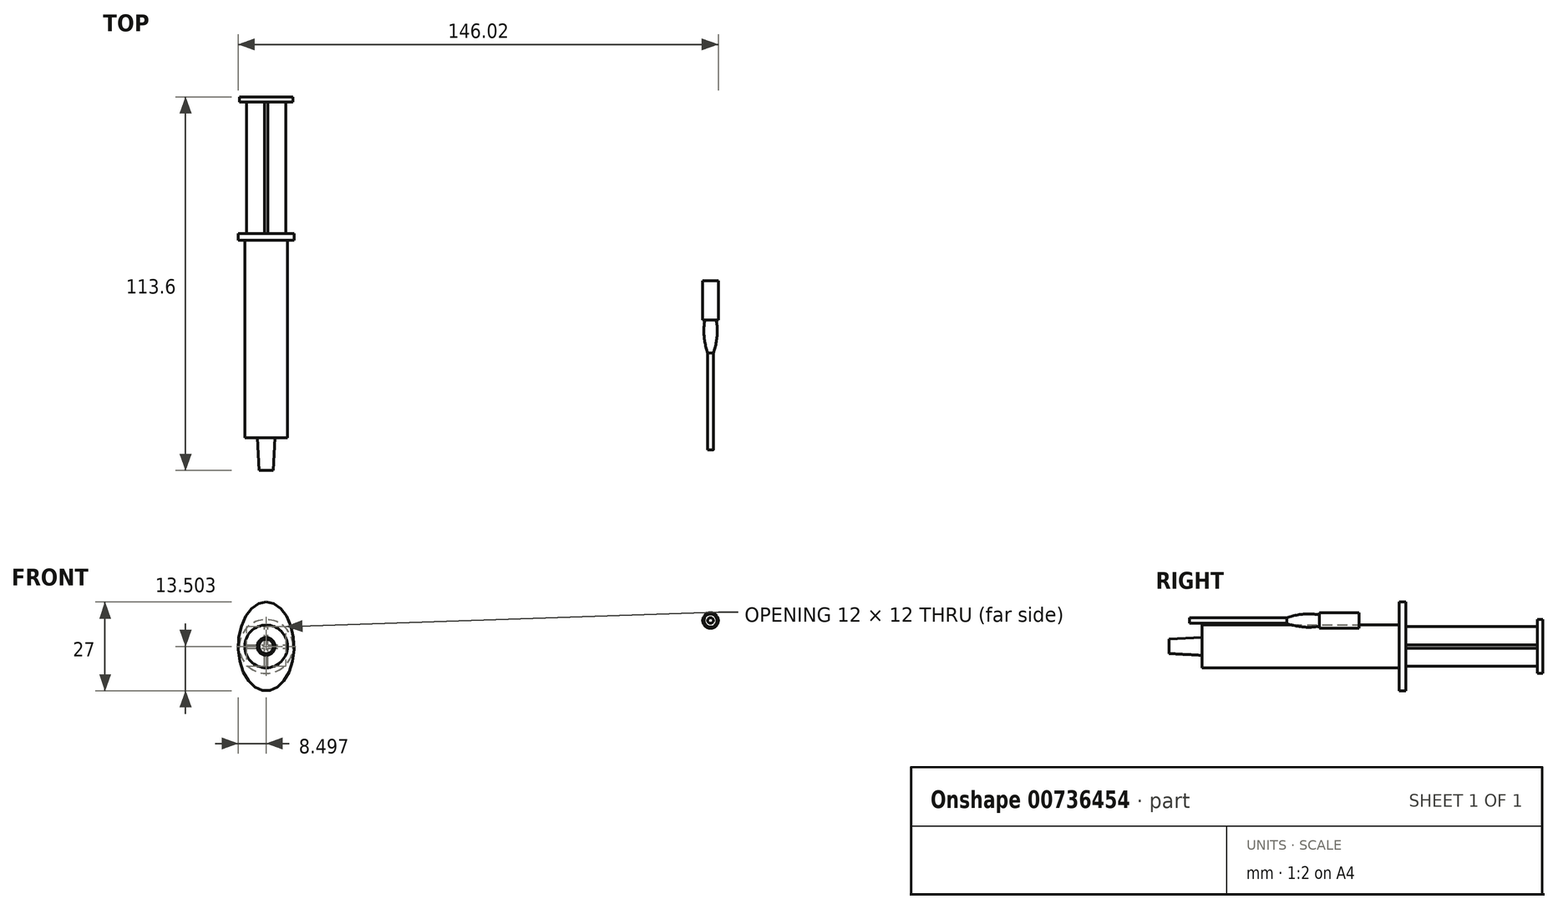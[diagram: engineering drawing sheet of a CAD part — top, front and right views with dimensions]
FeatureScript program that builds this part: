
annotation { "Feature Type Name" : "Feature", "Feature Type Description" : "" }
export const myFeature = defineFeature(function(context is Context, id is Id, definition is map)
    precondition{}
    {
        {
            var Q0;
            Q0=qCreatedBy(makeId("Front.planeOp"),FACE);
            var sketch = newSketch(context, id + "F0", { "sketchPlane" : qUnion([Q0])});
            skEllipse(sketch, "E0", {"center": v(-135.14, -7.87) * mm, "majorRadius": 13.5 * mm, "minorRadius": 8.5 * mm, "majorAxis": v(0, 1)});
            skCircle(sketch, "E1", {"center": v(-135.14, -7.87) * mm, "radius": 6.5 * mm});
            skLineSegment(sketch, "E2", {"start": v(-143.64, -7.87) * mm, "end": v(-126.64, -7.87) * mm, "construction": true});
            skLineSegment(sketch, "E3", {"start": v(-135.14, 5.63) * mm, "end": v(-135.14, -21.37) * mm, "construction": true});
            skSolve(sketch);
        }
        {
            var Q0;
            Q0=makeQuery(id+"F0.imprint","IMPRINT",FACE,{"disambiguationData":[TD([[makeQuery(id+"F0.imprint","IMPRINT",EDGE,{"derivedFrom":sQuery(id+"F0.wireOp",EDGE,"E0")}),1.0]])]});
            var Q1;
            Q1=makeQuery(id+"F0.imprint","IMPRINT",FACE,{"disambiguationData":[TD([[makeQuery(id+"F0.imprint","IMPRINT",EDGE,{"derivedFrom":sQuery(id+"F0.wireOp",EDGE,"E1")}),1.0]])]});
            extrude(context, id + "F1", {"entities" : qUnion([Q0, Q1]), "oppositeDirection" : true, "depth" : 2 * mm, "offsetDistance" : 25 * mm});
        }
        {
            var Q0;
            Q0=makeQuery(id+"F0.imprint","IMPRINT",FACE,{"disambiguationData":[TD([[makeQuery(id+"F0.imprint","IMPRINT",EDGE,{"derivedFrom":sQuery(id+"F0.wireOp",EDGE,"E1")}),1.0]])]});
            extrude(context, id + "F2", {"entities" : qUnion([Q0]), "operationType" : NewBodyOperationType.ADD, "depth" : 60 * mm, "offsetDistance" : 25 * mm});
        }
        {
            var Q0;
            Q0=makeQuery(id+"F1.opExtrude","CAP_FACE",FACE,{"disambiguationData":[OSD([sQuery(id+"F0.wireOp",EDGE,"E0")])],"isStart":false});
            var sketch = newSketch(context, id + "F3", { "sketchPlane" : qUnion([Q0])});
            skLineSegment(sketch, "E4.bottom", {"start": v(141.14, -7.37) * mm, "end": v(129.14, -7.37) * mm});
            skLineSegment(sketch, "E4.top", {"start": v(141.14, -8.37) * mm, "end": v(129.14, -8.37) * mm});
            skLineSegment(sketch, "E4.left", {"start": v(141.14, -7.37) * mm, "end": v(141.14, -8.37) * mm});
            skLineSegment(sketch, "E4.right", {"start": v(129.14, -7.37) * mm, "end": v(129.14, -8.37) * mm});
            skPoint(sketch, "E4.middle", {"position": v(135.14, -7.87) * mm});
            skLineSegment(sketch, "E5.bottom", {"start": v(135.64, -13.87) * mm, "end": v(134.64, -13.87) * mm});
            skLineSegment(sketch, "E5.top", {"start": v(135.64, -1.87) * mm, "end": v(134.64, -1.87) * mm});
            skLineSegment(sketch, "E5.left", {"start": v(135.64, -13.87) * mm, "end": v(135.64, -1.87) * mm});
            skLineSegment(sketch, "E5.right", {"start": v(134.64, -13.87) * mm, "end": v(134.64, -1.87) * mm});
            skSolve(sketch);
        }
        {
            var Q0;
            {var subQ0=sQuery(id+"F3.wireOp",EDGE,"E5.left");var subQ1=sQuery(id+"F3.wireOp",EDGE,"E4.bottom");var subQ2=makeQuery(id+"F3.imprint","INTERSECT",VERTEX,{"derivedFrom":[subQ1,subQ0]});Q0=makeQuery(id+"F3.imprint","IMPRINT",FACE,{"disambiguationData":[TD([[makeQuery(id+"F3.imprint","IMPRINT",EDGE,{"disambiguationData":[TD([[subQ2,-1.0]])],"derivedFrom":subQ1}),1.0]])]});}
            var Q1;
            {var subQ5=sQuery(id+"F3.wireOp",EDGE,"E5.top");Q1=makeQuery(id+"F3.imprint","IMPRINT",FACE,{"disambiguationData":[TD([[makeQuery(id+"F3.imprint","IMPRINT",EDGE,{"derivedFrom":subQ5}),1.0]])]});}
            var Q2;
            {var subQ0=sQuery(id+"F3.wireOp",EDGE,"E4.left");Q2=makeQuery(id+"F3.imprint","IMPRINT",FACE,{"disambiguationData":[TD([[makeQuery(id+"F3.imprint","IMPRINT",EDGE,{"derivedFrom":subQ0}),-1.0]])]});}
            var Q3;
            {var subQ5=sQuery(id+"F3.wireOp",EDGE,"E5.bottom");Q3=makeQuery(id+"F3.imprint","IMPRINT",FACE,{"disambiguationData":[TD([[makeQuery(id+"F3.imprint","IMPRINT",EDGE,{"derivedFrom":subQ5}),-1.0]])]});}
            var Q4;
            {var subQ0=sQuery(id+"F3.wireOp",EDGE,"E4.right");Q4=makeQuery(id+"F3.imprint","IMPRINT",FACE,{"disambiguationData":[TD([[makeQuery(id+"F3.imprint","IMPRINT",EDGE,{"derivedFrom":subQ0}),1.0]])]});}
            extrude(context, id + "F4", {"entities" : qUnion([Q0, Q1, Q2, Q3, Q4]), "operationType" : NewBodyOperationType.ADD, "depth" : 40 * mm, "offsetDistance" : 25 * mm});
        }
        {
            var Q0;
            Q0=makeQuery(id+"F4.opExtrude","CAP_FACE",FACE,{"disambiguationData":[OSD([sQuery(id+"F3.wireOp",EDGE,"E4.bottom"),sQuery(id+"F3.wireOp",EDGE,"E4.top"),sQuery(id+"F3.wireOp",EDGE,"E4.left"),sQuery(id+"F3.wireOp",EDGE,"E4.right"),sQuery(id+"F3.wireOp",EDGE,"E5.bottom"),sQuery(id+"F3.wireOp",EDGE,"E5.top"),sQuery(id+"F3.wireOp",EDGE,"E5.left"),sQuery(id+"F3.wireOp",EDGE,"E5.right")])],"isStart":false});
            var sketch = newSketch(context, id + "F5", { "sketchPlane" : qUnion([Q0])});
            skCircle(sketch, "E6", {"center": v(135.14, -7.87) * mm, "radius": 8.17 * mm});
            skSolve(sketch);
        }
        {
            var Q0;
            Q0=makeQuery(id+"F5.imprint","IMPRINT",FACE,{"disambiguationData":[TD([[makeQuery(id+"F5.imprint","IMPRINT",EDGE,{"derivedFrom":sQuery(id+"F5.wireOp",EDGE,"E6")}),1.0]])]});
            var Q1;
            {var subQ8=sQuery(id+"F3.wireOp",EDGE,"E4.left");Q1=makeQuery(id+"F5.imprint","IMPRINT",FACE,{"disambiguationData":[TD([[makeQuery(id+"F5.imprint","IMPRINT",EDGE,{"derivedFrom":makeQuery(id+"F4.opExtrude","CAP_EDGE",EDGE,{"disambiguationData":[OSD([subQ8])],"isStart":false})}),-1.0]])]});}
            extrude(context, id + "F6", {"entities" : qUnion([Q0, Q1]), "operationType" : NewBodyOperationType.ADD, "depth" : 1.6 * mm, "offsetDistance" : 25 * mm});
        }
        {
            var Q0;
            Q0=makeQuery(id+"F2.opExtrude","CAP_FACE",FACE,{"disambiguationData":[OSD([sQuery(id+"F0.wireOp",EDGE,"E1")])],"isStart":false});
            var sketch = newSketch(context, id + "F7", { "sketchPlane" : qUnion([Q0])});
            skCircle(sketch, "E7", {"center": v(-135.14, -7.87) * mm, "radius": 2.7 * mm});
            skSolve(sketch);
        }
        {
            var Q0;
            Q0=makeQuery(id+"F7.imprint","IMPRINT",FACE,{"disambiguationData":[TD([[makeQuery(id+"F7.imprint","IMPRINT",EDGE,{"derivedFrom":sQuery(id+"F7.wireOp",EDGE,"E7")}),1.0]])]});
            extrude(context, id + "F8", {"entities" : qUnion([Q0]), "operationType" : NewBodyOperationType.ADD, "depth" : 10 * mm, "offsetDistance" : 25 * mm, "hasDraft" : true, "draftAngle" : 3 * degree, "draftPullDirection" : true});
        }
        {
            var Q0;
            Q0=qCreatedBy(makeId("Top.planeOp"),FACE);
            var sketch = newSketch(context, id + "F9", { "sketchPlane" : qUnion([Q0])});
            skLineSegment(sketch, "E8", {"start": v(0, 0) * mm, "end": v(0, -63.75) * mm, "construction": true});
            skLineSegment(sketch, "E9", {"start": v(0.86, -63.75) * mm, "end": v(0.86, -34.24) * mm});
            skArc(sketch, "E10", {"start": v(0.86, -34.24) * mm, "mid": v(1.94, -29.3) * mm, "end": v(1.75, -24.24) * mm});
            skLineSegment(sketch, "E11", {"start": v(0.86, -63.75) * mm, "end": v(0, -63.75) * mm});
            skLineSegment(sketch, "E12", {"start": v(0, -63.75) * mm, "end": v(0, -24.24) * mm});
            skLineSegment(sketch, "E13", {"start": v(0, -24.24) * mm, "end": v(1.75, -24.24) * mm});
            skLineSegment(sketch, "E14.bottom", {"start": v(0, -24.24) * mm, "end": v(2.37, -24.24) * mm});
            skLineSegment(sketch, "E14.top", {"start": v(0, -12.24) * mm, "end": v(2.37, -12.24) * mm});
            skLineSegment(sketch, "E14.left", {"start": v(0, -24.24) * mm, "end": v(0, -12.24) * mm});
            skLineSegment(sketch, "E14.right", {"start": v(2.37, -24.24) * mm, "end": v(2.37, -12.24) * mm});
            skSolve(sketch);
        }
        {
            var Q0;
            Q0=makeQuery(id+"F9.imprint","IMPRINT",FACE,{"disambiguationData":[TD([[makeQuery(id+"F9.imprint","IMPRINT",EDGE,{"derivedFrom":sQuery(id+"F9.wireOp",EDGE,"E14.top")}),-1.0]])]});
            var Q1;
            Q1=makeQuery(id+"F9.imprint","IMPRINT",FACE,{"disambiguationData":[TD([[makeQuery(id+"F9.imprint","IMPRINT",EDGE,{"derivedFrom":sQuery(id+"F9.wireOp",EDGE,"E9")}),1.0]])]});
            var Q2;
            Q2=sQuery(id+"F9.wireOp",EDGE,"E8");
            revolve(context, id + "F10", {"surfaceOperationType" : NewSurfaceOperationType.NEW, "entities" : qUnion([Q0, Q1]), "axis" : qUnion([Q2]), "revolveType" : RevolveType.FULL});
        }
    });
